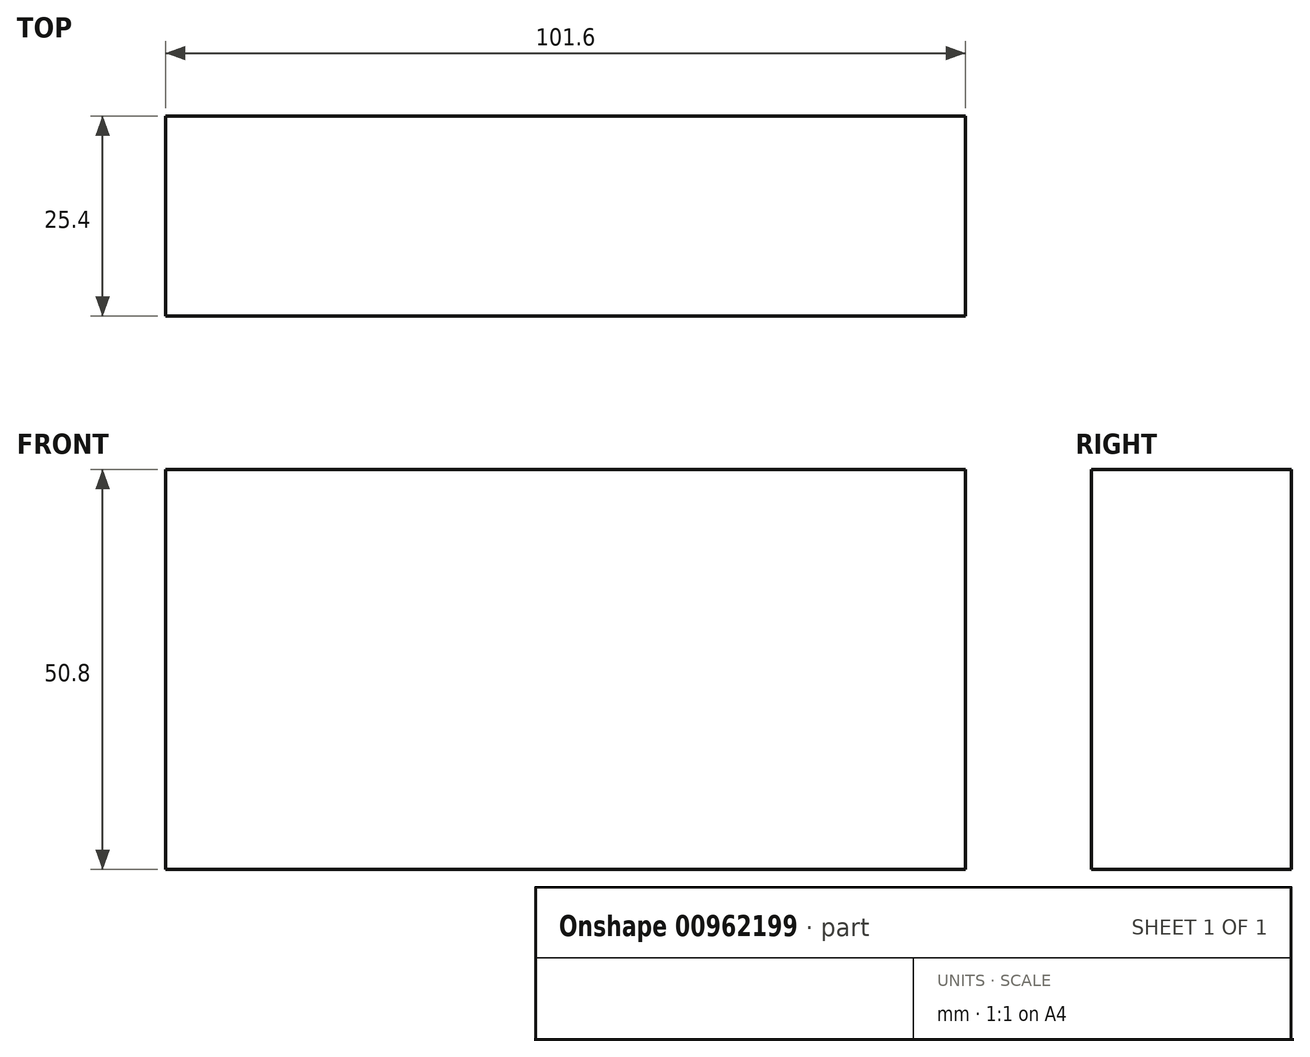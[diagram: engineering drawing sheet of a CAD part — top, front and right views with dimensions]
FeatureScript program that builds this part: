
annotation { "Feature Type Name" : "Feature", "Feature Type Description" : "" }
export const myFeature = defineFeature(function(context is Context, id is Id, definition is map)
    precondition{}
    {
        {
            var Q0;
            Q0=qCreatedBy(makeId("Front.planeOp"),FACE);
            var sketch = newSketch(context, id + "F0", { "sketchPlane" : qUnion([Q0])});
            skLineSegment(sketch, "E0", {"start": v(101.6, 0) * mm, "end": v(0, 0) * mm});
            skLineSegment(sketch, "E1", {"start": v(0, 0) * mm, "end": v(0, -50.8) * mm});
            skLineSegment(sketch, "E2", {"start": v(0, -50.8) * mm, "end": v(0, -50.8) * mm});
            skLineSegment(sketch, "E3", {"start": v(92.3, -50.8) * mm, "end": v(101.6, -50.8) * mm});
            skLineSegment(sketch, "E4", {"start": v(0, -50.8) * mm, "end": v(92.3, -50.8) * mm});
            skLineSegment(sketch, "E5", {"start": v(101.6, -50.8) * mm, "end": v(101.6, 0) * mm});
            skSolve(sketch);
        }
        {
            var Q0;
            Q0=makeQuery(id+"F0.imprint","IMPRINT",FACE,{"disambiguationData":[TD([[makeQuery(id+"F0.imprint","IMPRINT",EDGE,{"derivedFrom":sQuery(id+"F0.wireOp",EDGE,"E0")}),1.0]])]});
            extrude(context, id + "F1", {"entities" : qUnion([Q0]), "depth" : 25.4 * mm, "offsetDistance" : 25.4 * mm});
        }
    });
